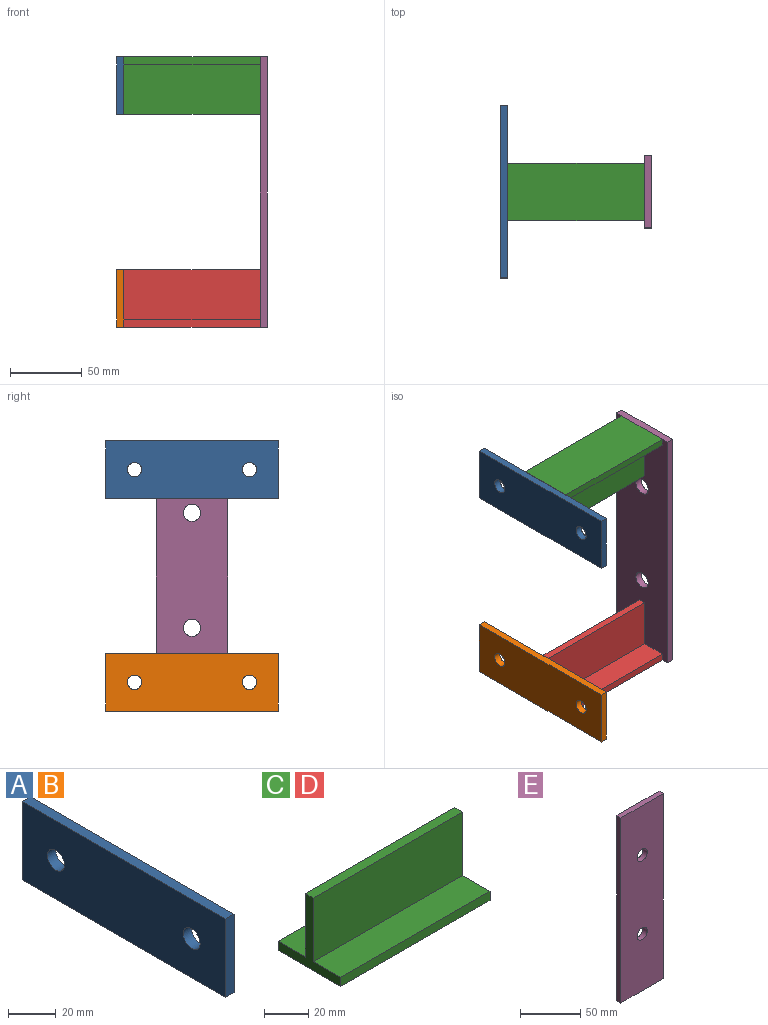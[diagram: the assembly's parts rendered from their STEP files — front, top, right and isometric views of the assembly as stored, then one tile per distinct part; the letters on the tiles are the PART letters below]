
ASSEMBLY  parts=5 mates=4
PART A: 8 faces, bbox 5x120x40 mm
  f0: plane 120x5mm, normal (0,0,1), area 600mm2, adj f1,f3,f4,f5
  f1: plane 40x5mm, normal (0,-1,0), area 200mm2, adj f0,f2,f4,f5
  f2: plane 120x5mm, normal (0,0,-1), area 600mm2, adj f1,f3,f4,f5
  f3: plane 40x5mm, normal (0,1,0), area 200mm2, adj f0,f2,f4,f5
  f4: plane 120x40mm, normal (-1,0,0), area 4642.9mm2, adj f0,f1,f2,f3,f6,f7
  f5: plane 120x40mm, normal (1,0,0), area 4642.9mm2, adj f0,f1,f2,f3,f6,f7
  f6: cylinder r=5mm len=10mm, axis (1,0,0), area 157.1mm2, adj f4,f5
  f7: cylinder r=5mm len=10mm, axis (1,0,0), area 157.1mm2, adj f4,f5
PART B: same geometry as A
PART C: 10 faces, bbox 95x40x40 mm
  f0: plane 95x17.5mm, normal (0,0,1), area 1662.5mm2, adj f1,f7,f8,f9
  f1: plane 95x35mm, normal (0,1,0), area 3325mm2, adj f0,f2,f8,f9
  f2: plane 95x5mm, normal (0,0,1), area 475mm2, adj f1,f3,f8,f9
  f3: plane 95x35mm, normal (0,-1,0), area 3325mm2, adj f2,f4,f8,f9
  f4: plane 95x17.5mm, normal (0,0,1), area 1662.5mm2, adj f3,f5,f8,f9
  f5: plane 95x5mm, normal (0,-1,0), area 475mm2, adj f4,f6,f8,f9
  f6: plane 95x40mm, normal (0,0,-1), area 3800mm2, adj f5,f7,f8,f9
  f7: plane 95x5mm, normal (0,1,0), area 475mm2, adj f0,f6,f8,f9
  f8: plane 40x40mm, normal (1,0,0), area 375mm2, adj f0,f1,f2,f3,f4,f5,f6,f7
  f9: plane 40x40mm, normal (-1,0,0), area 375mm2, adj f0,f1,f2,f3,f4,f5,f6,f7
PART D: same geometry as C
PART E: 8 faces, bbox 50x5x188 mm
  f0: plane 50x5mm, normal (0,0,1), area 250mm2, adj f1,f3,f4,f5
  f1: plane 188x5mm, normal (-1,0,0), area 940mm2, adj f0,f2,f4,f5
  f2: plane 50x5mm, normal (0,0,-1), area 250mm2, adj f1,f3,f4,f5
  f3: plane 188x5mm, normal (1,0,0), area 940mm2, adj f0,f2,f4,f5
  f4: plane 188x50mm, normal (0,-1,0), area 9173.8mm2, adj f0,f1,f2,f3,f6,f7
  f5: plane 188x50mm, normal (0,1,0), area 9173.8mm2, adj f0,f1,f2,f3,f6,f7
  f6: cylinder r=6mm len=12mm, axis (0,-1,0), area 188.5mm2, adj f4,f5
  f7: cylinder r=6mm len=12mm, axis (0,-1,0), area 188.5mm2, adj f4,f5
PLACE A t=(62.63,-75.56,100.71)mm
PLACE B t=(62.63,-75.56,-47.29)mm
PLACE C rot(axis=(1,0,0),180deg) t=(62.63,-75.56,118.21)mm
PLACE D t=(62.63,-75.56,-64.79)mm
PLACE E rot(axis=(0,0,1),90deg) t=(157.63,-75.56,26.71)mm
MATE fastened C.f9 <-> A.f5  axis (-1,0,0) through (62.63,-75.56,120.71)mm
MATE fastened D.f9 <-> B.f5  axis (-1,0,0) through (62.63,-75.56,-67.29)mm
MATE fastened E.f5 <-> C.f8  axis (-1,0,0) through (157.63,-75.56,120.71)mm
MATE fastened D.f8 <-> E.f5  axis (1,0,0) through (157.63,-75.56,-67.29)mm
